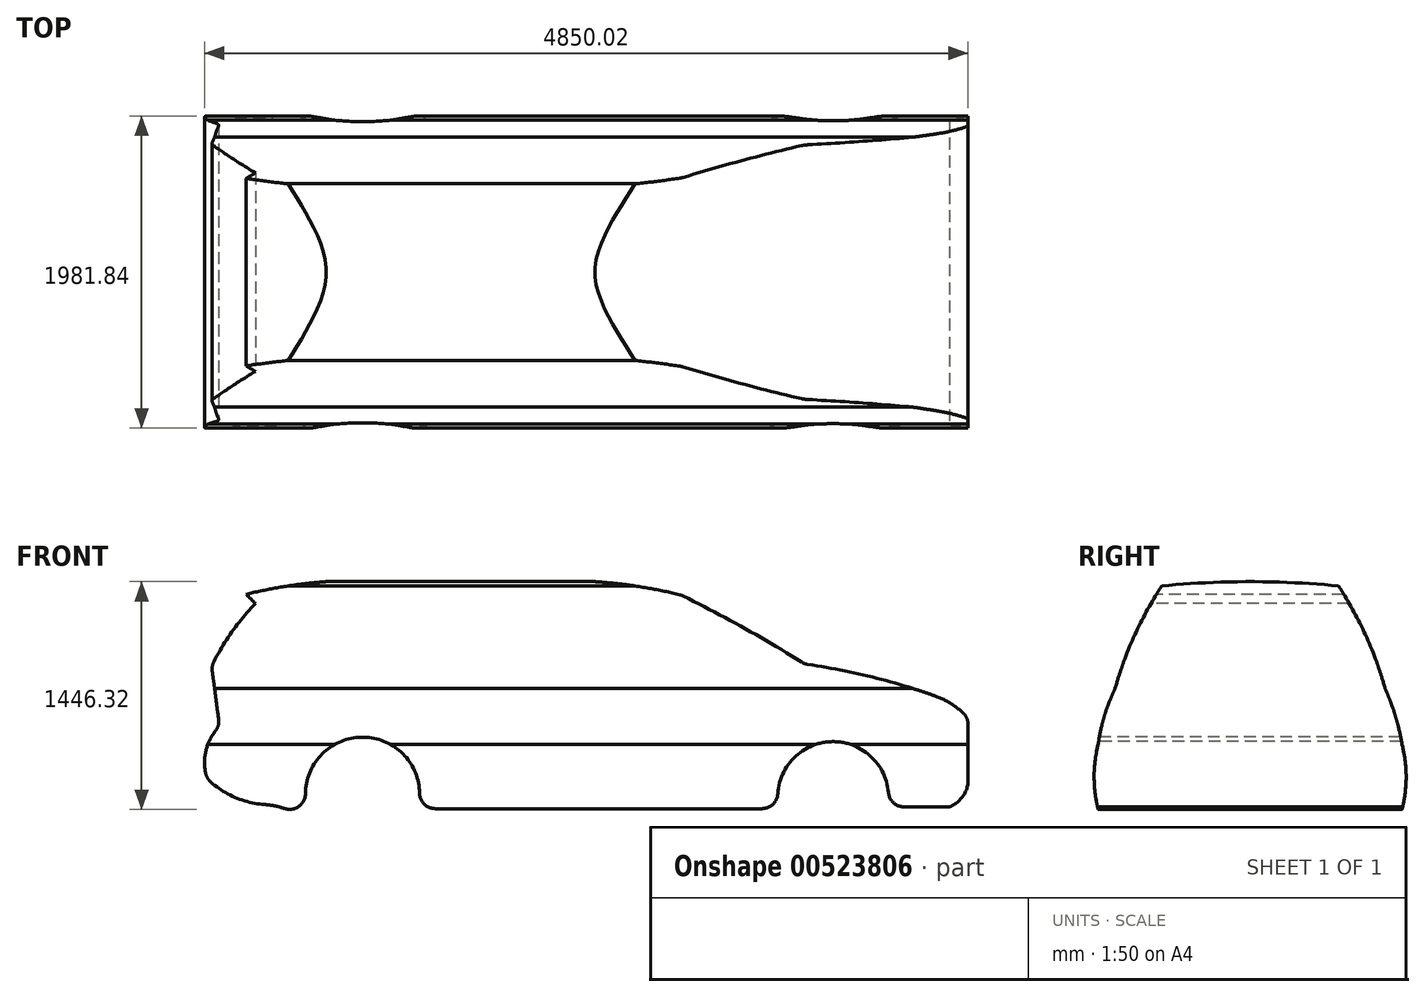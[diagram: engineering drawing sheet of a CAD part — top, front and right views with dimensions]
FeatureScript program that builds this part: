
annotation { "Feature Type Name" : "Feature", "Feature Type Description" : "" }
export const myFeature = defineFeature(function(context is Context, id is Id, definition is map)
    precondition{}
    {
        {
            var Q0;
            Q0=qCreatedBy(makeId("Front.planeOp"),FACE);
            var sketch = newSketch(context, id + "F0", { "sketchPlane" : qUnion([Q0])});
            skArc(sketch, "E0", {"start": v(1392.2, 284.3) * mm, "mid": v(1032.18, 738.5) * mm, "end": v(696.62, 265.94) * mm});
            skArc(sketch, "E1", {"start": v(4377.36, 295.76) * mm, "mid": v(4024.76, 710.08) * mm, "end": v(3686.08, 284.3) * mm});
            skArc(sketch, "E2", {"start": v(361.36, 1587.13) * mm, "mid": v(206.68, 1399.51) * mm, "end": v(83.01, 1190.14) * mm});
            skLineSegment(sketch, "E3", {"start": v(361.36, 1587.13) * mm, "end": v(302.04, 1646.45) * mm});
            skArc(sketch, "E4", {"start": v(940.88, 1733.15) * mm, "mid": v(619.25, 1706.1) * mm, "end": v(302.04, 1646.45) * mm});
            skLineSegment(sketch, "E5", {"start": v(940.88, 1733.15) * mm, "end": v(2309.83, 1733.15) * mm});
            skArc(sketch, "E6", {"start": v(3067.77, 1640.1) * mm, "mid": v(2691.65, 1709.8) * mm, "end": v(2309.83, 1733.15) * mm});
            skArc(sketch, "E7", {"start": v(3847.6, 1203.83) * mm, "mid": v(3463.53, 1432.4) * mm, "end": v(3067.77, 1640.1) * mm});
            skArc(sketch, "E8", {"start": v(4682.66, 998.49) * mm, "mid": v(4270.35, 1122.37) * mm, "end": v(3847.6, 1203.83) * mm});
            skArc(sketch, "E9", {"start": v(4888, 857.03) * mm, "mid": v(4794.69, 941.34) * mm, "end": v(4682.66, 998.49) * mm});
            skLineSegment(sketch, "E10", {"start": v(4888, 857.03) * mm, "end": v(4888, 469.16) * mm});
            skArc(sketch, "E11", {"start": v(4769.36, 295.76) * mm, "mid": v(4855.5, 364.11) * mm, "end": v(4888, 469.16) * mm});
            skLineSegment(sketch, "E12", {"start": v(4769.36, 295.76) * mm, "end": v(4377.36, 295.76) * mm});
            skLineSegment(sketch, "E13", {"start": v(3686.08, 284.3) * mm, "end": v(1392.2, 284.3) * mm});
            skArc(sketch, "E14", {"start": v(484.57, 309.45) * mm, "mid": v(587.96, 274.85) * mm, "end": v(696.62, 265.94) * mm});
            skLineSegment(sketch, "E15", {"start": v(83.01, 1190.14) * mm, "end": v(133.2, 806.84) * mm});
            skArc(sketch, "E16", {"start": v(133.2, 806.84) * mm, "mid": v(46.35, 651.47) * mm, "end": v(55.63, 473.73) * mm});
            skArc(sketch, "E17", {"start": v(55.63, 473.73) * mm, "mid": v(253.23, 347.53) * mm, "end": v(484.57, 309.45) * mm});
            skSolve(sketch);
        }
        {
            var Q0;
            Q0=makeQuery(id+"F0.imprint","IMPRINT",FACE,{"disambiguationData":[TD([[makeQuery(id+"F0.imprint","IMPRINT",EDGE,{"derivedFrom":sQuery(id+"F0.wireOp",EDGE,"E0")}),-1.0]])]});
            extrude(context, id + "F1", {"entities" : qUnion([Q0]), "oppositeDirection" : true, "depth" : 2000 * mm, "offsetDistance" : 25 * mm});
        }
        {
            var Q0;
            Q0=qCreatedBy(makeId("Right.planeOp"),FACE);
            var sketch = newSketch(context, id + "F2", { "sketchPlane" : qUnion([Q0])});
            skArc(sketch, "E18", {"start": v(78.76, 152.01) * mm, "mid": v(1000, 79.67) * mm, "end": v(1921.24, 152.01) * mm});
            skArc(sketch, "E19", {"start": v(34.8, 691.57) * mm, "mid": v(11.84, 418.13) * mm, "end": v(78.76, 152.01) * mm});
            skArc(sketch, "E20", {"start": v(142.71, 1047.27) * mm, "mid": v(74.63, 873.7) * mm, "end": v(34.8, 691.57) * mm});
            skArc(sketch, "E21", {"start": v(438.47, 1698.73) * mm, "mid": v(265.28, 1384.49) * mm, "end": v(142.71, 1047.27) * mm});
            skArc(sketch, "E22", {"start": v(1561.53, 1698.73) * mm, "mid": v(1000, 1726.26) * mm, "end": v(438.47, 1698.73) * mm});
            skPoint(sketch, "E23.startSnap0", {"position": v(1000, 1726.26) * mm});
            skPoint(sketch, "E23.endSnap0", {"position": v(1000, 1726.26) * mm});
            skArc(sketch, "E24.MirrorCS", {"start": v(1965.2, 691.57) * mm, "mid": v(1988.16, 418.13) * mm, "end": v(1921.24, 152.01) * mm});
            skArc(sketch, "E25.MirrorCS", {"start": v(1561.53, 1698.73) * mm, "mid": v(1734.72, 1384.49) * mm, "end": v(1857.29, 1047.27) * mm});
            skArc(sketch, "E26", {"start": v(1965.2, 691.57) * mm, "mid": v(1922.46, 872.82) * mm, "end": v(1857.29, 1047.27) * mm});
            skLineSegment(sketch, "E27.bottom", {"start": v(2032.1, 1781.94) * mm, "end": v(-43.46, 1781.94) * mm});
            skLineSegment(sketch, "E27.top", {"start": v(2032.1, -40.61) * mm, "end": v(-43.46, -40.61) * mm});
            skLineSegment(sketch, "E27.left", {"start": v(2032.1, 1781.94) * mm, "end": v(2032.1, -40.61) * mm});
            skLineSegment(sketch, "E27.right", {"start": v(-43.46, 1781.94) * mm, "end": v(-43.46, -40.61) * mm});
            skSolve(sketch);
        }
        {
            var Q0;
            Q0 = qSketchRegion(id + "F2", true);
            extrude(context, id + "F3", {"entities" : qUnion([Q0]), "operationType" : NewBodyOperationType.REMOVE, "endBound" : BoundingType.THROUGH_ALL, "depth" : 25 * mm, "offsetDistance" : 25 * mm});
        }
        {
            var Q0;
            Q0=makeQuery(id+"F1.opExtrude","SWEPT_EDGE",EDGE,{"disambiguationData":[OSD([sQuery(id+"F0.wireOp",EDGE,"E0"),sQuery(id+"F0.wireOp",EDGE,"E14")])]});
            var Q1;
            Q1=makeQuery(id+"F1.opExtrude","SWEPT_EDGE",EDGE,{"disambiguationData":[OSD([sQuery(id+"F0.wireOp",EDGE,"E0"),sQuery(id+"F0.wireOp",EDGE,"E13")])]});
            var Q2;
            Q2=makeQuery(id+"F1.opExtrude","SWEPT_EDGE",EDGE,{"disambiguationData":[OSD([sQuery(id+"F0.wireOp",EDGE,"E1"),sQuery(id+"F0.wireOp",EDGE,"E13")])]});
            var Q3;
            Q3=makeQuery(id+"F1.opExtrude","SWEPT_EDGE",EDGE,{"disambiguationData":[OSD([sQuery(id+"F0.wireOp",EDGE,"E1"),sQuery(id+"F0.wireOp",EDGE,"E12")])]});
            var Q4;
            Q4=makeQuery(id+"F1.opExtrude","SWEPT_EDGE",EDGE,{"disambiguationData":[OSD([sQuery(id+"F0.wireOp",EDGE,"E7"),sQuery(id+"F0.wireOp",EDGE,"E8")])]});
            var Q5;
            Q5=makeQuery(id+"F1.opExtrude","SWEPT_EDGE",EDGE,{"disambiguationData":[OSD([sQuery(id+"F0.wireOp",EDGE,"E9"),sQuery(id+"F0.wireOp",EDGE,"E10")])]});
            var Q6;
            Q6=makeQuery(id+"F1.opExtrude","SWEPT_EDGE",EDGE,{"disambiguationData":[OSD([sQuery(id+"F0.wireOp",EDGE,"E6"),sQuery(id+"F0.wireOp",EDGE,"E7")])]});
            var Q7;
            Q7=makeQuery(id+"F1.opExtrude","SWEPT_EDGE",EDGE,{"disambiguationData":[OSD([sQuery(id+"F0.wireOp",EDGE,"E2"),sQuery(id+"F0.wireOp",EDGE,"E15")])]});
            var Q8;
            Q8=makeQuery(id+"F1.opExtrude","SWEPT_EDGE",EDGE,{"disambiguationData":[OSD([sQuery(id+"F0.wireOp",EDGE,"E15"),sQuery(id+"F0.wireOp",EDGE,"E16")])]});
            var Q9;
            Q9=makeQuery(id+"F1.opExtrude","SWEPT_EDGE",EDGE,{"disambiguationData":[OSD([sQuery(id+"F0.wireOp",EDGE,"E16"),sQuery(id+"F0.wireOp",EDGE,"E17")])]});
            fillet(context, id + "F4", {"entities" : qUnion([Q0, Q1, Q2, Q3, Q4, Q5, Q6, Q7, Q8, Q9]), "radius" : 100 * mm, "tangentPropagation" : true, "allowEdgeOverflow" : false});
        }
        {
            var Q0;
            Q0=makeQuery(id+"F1.opExtrude","SWEPT_EDGE",EDGE,{"disambiguationData":[OSD([sQuery(id+"F0.wireOp",EDGE,"E14"),sQuery(id+"F0.wireOp",EDGE,"E17")])]});
            fillet(context, id + "F5", {"entities" : qUnion([Q0]), "radius" : 500 * mm, "tangentPropagation" : true, "allowEdgeOverflow" : false});
        }
    });
